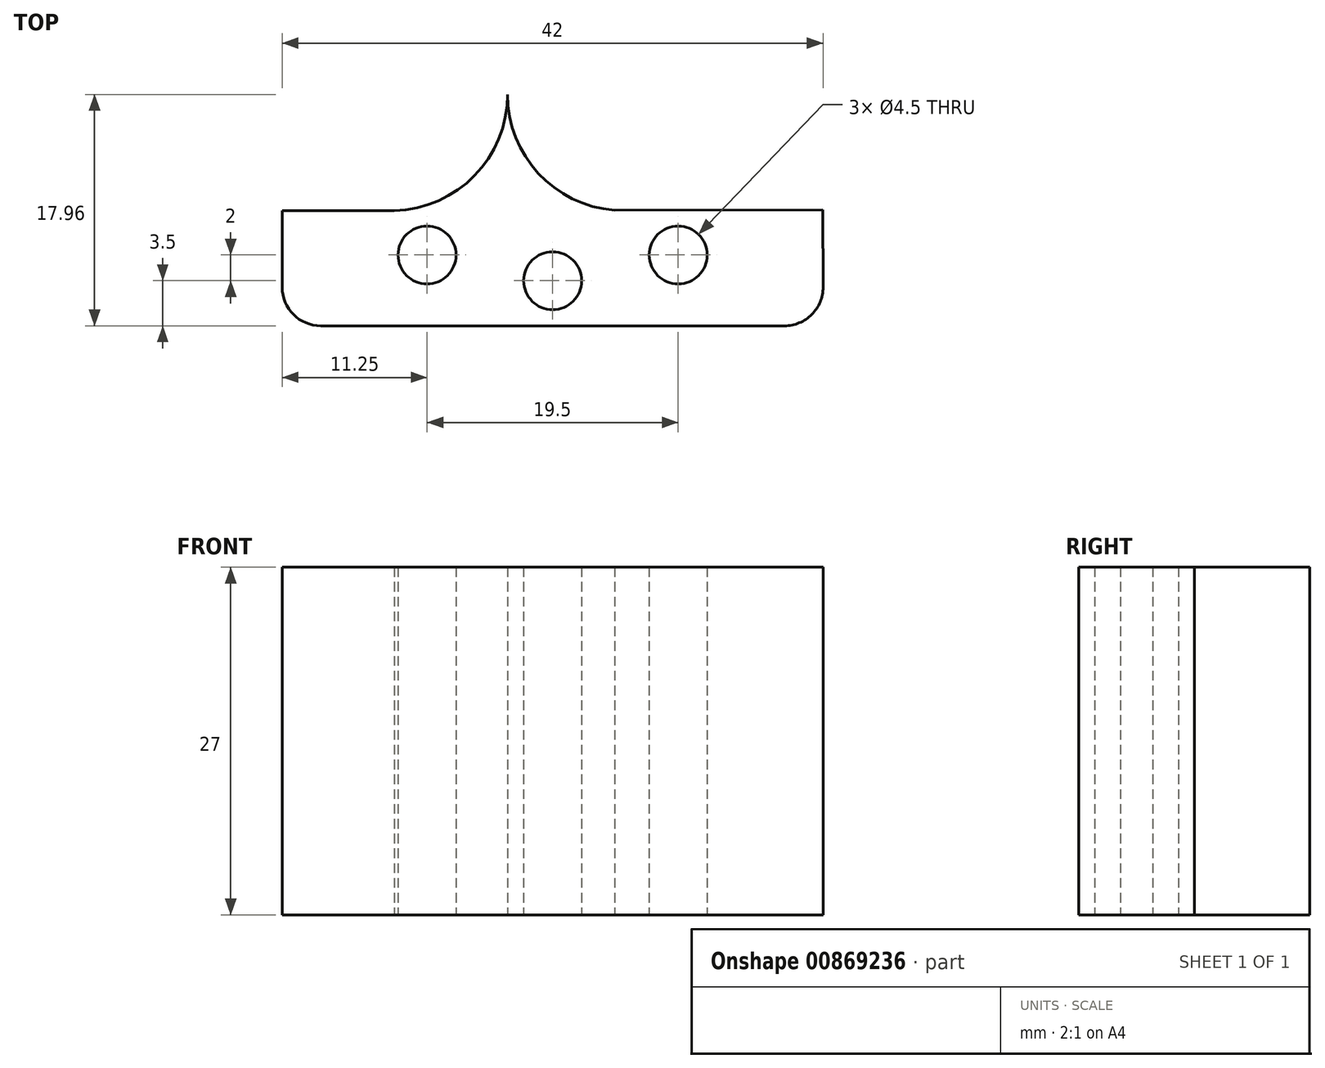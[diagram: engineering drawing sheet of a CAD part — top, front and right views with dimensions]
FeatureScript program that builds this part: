
annotation { "Feature Type Name" : "Feature", "Feature Type Description" : "" }
export const myFeature = defineFeature(function(context is Context, id is Id, definition is map)
    precondition{}
    {
        {
            var Q0;
            Q0=qCreatedBy(makeId("Top.planeOp"),FACE);
            var sketch = newSketch(context, id + "F0", { "sketchPlane" : qUnion([Q0])});
            skLineSegment(sketch, "E0.top", {"start": v(-21, -3.5) * mm, "end": v(21, -3.5) * mm});
            skLineSegment(sketch, "E0.left", {"start": v(-21, 1) * mm, "end": v(-21, -3.5) * mm});
            skLineSegment(sketch, "E0.right", {"start": v(21, 1) * mm, "end": v(21, -3.5) * mm});
            skCircle(sketch, "E1", {"center": v(0, 0) * mm, "radius": 2.25 * mm});
            skCircle(sketch, "E2", {"center": v(9.75, 2) * mm, "radius": 2.25 * mm});
            skCircle(sketch, "E3.MirrorC", {"center": v(-9.75, 2) * mm, "radius": 2.25 * mm});
            skPoint(sketch, "E4.orphan", {"position": v(21, 5.5) * mm});
            skLineSegment(sketch, "E5", {"start": v(21, 5.5) * mm, "end": v(21, 1) * mm});
            skLineSegment(sketch, "E6", {"start": v(21, 5.5) * mm, "end": v(-21, 5.44) * mm});
            skLineSegment(sketch, "E7", {"start": v(-21, 1) * mm, "end": v(-21, 5.44) * mm});
            skLineSegment(sketch, "E8", {"start": v(-3.5, 5.46) * mm, "end": v(-3.5, 14.46) * mm, "construction": true});
            skArc(sketch, "E9", {"start": v(-3.5, 14.46) * mm, "mid": v(-0.6, 7.83) * mm, "end": v(6.25, 5.48) * mm});
            skArc(sketch, "E10.MirrorCS", {"start": v(-3.5, 14.46) * mm, "mid": v(-6.4, 7.83) * mm, "end": v(-13.25, 5.48) * mm});
            skSolve(sketch);
        }
        {
            var Q0;
            Q0 = qSketchRegion(id + "F0", true);
            extrude(context, id + "F1", {"entities" : qUnion([Q0]), "depth" : 27 * mm, "offsetDistance" : 25 * mm});
        }
        {
            var Q0;
            Q0=makeQuery(id+"F1.opExtrude","SWEPT_EDGE",EDGE,{"disambiguationData":[OSD([sQuery(id+"F0.wireOp",EDGE,"E0.top"),sQuery(id+"F0.wireOp",EDGE,"E0.right")])]});
            var Q1;
            Q1=makeQuery(id+"F1.opExtrude","SWEPT_EDGE",EDGE,{"disambiguationData":[OSD([sQuery(id+"F0.wireOp",EDGE,"E0.top"),sQuery(id+"F0.wireOp",EDGE,"E0.left")])]});
            fillet(context, id + "F2", {"entities" : qUnion([Q0, Q1]), "radius" : 3 * mm, "tangentPropagation" : true, "allowEdgeOverflow" : false});
        }
    });
